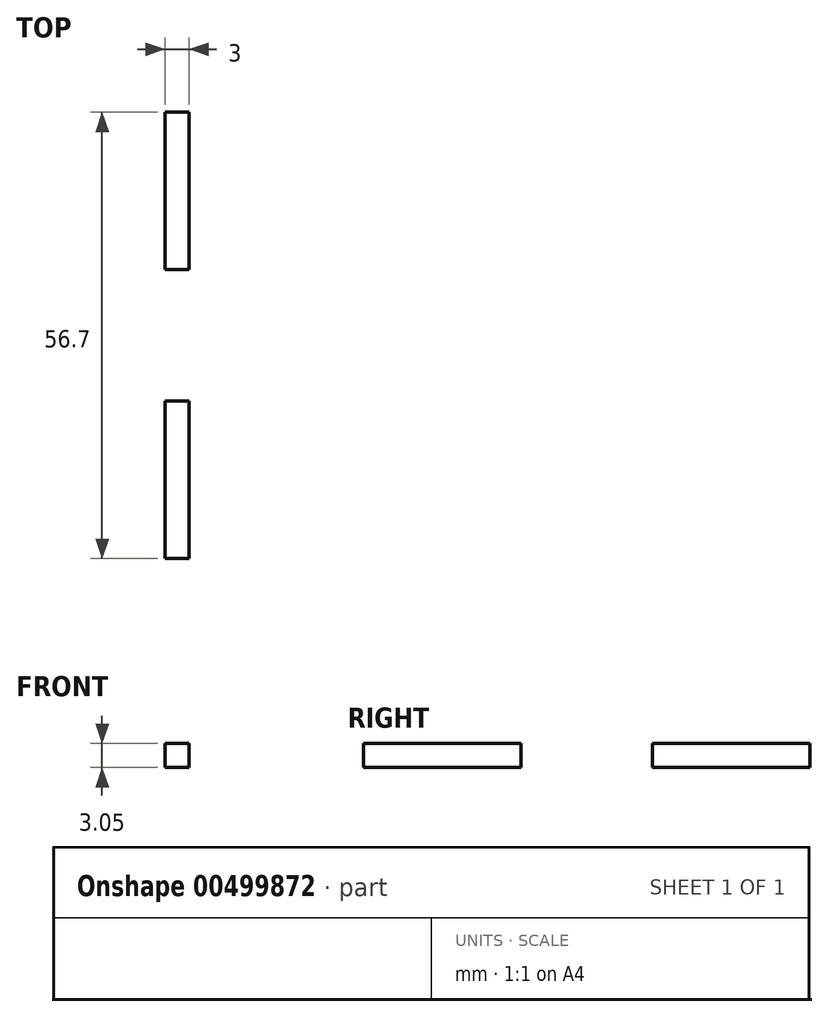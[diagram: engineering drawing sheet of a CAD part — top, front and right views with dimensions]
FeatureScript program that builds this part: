
annotation { "Feature Type Name" : "Feature", "Feature Type Description" : "" }
export const myFeature = defineFeature(function(context is Context, id is Id, definition is map)
    precondition{}
    {
        {
            var Q0;
            Q0=qCreatedBy(makeId("Right.planeOp"),FACE);
            var sketch = newSketch(context, id + "F0", { "sketchPlane" : qUnion([Q0])});
            skLineSegment(sketch, "E0.bottom", {"start": v(45, -45) * mm, "end": v(-45, -45) * mm});
            skLineSegment(sketch, "E0.top", {"start": v(45, 45) * mm, "end": v(-45, 45) * mm});
            skLineSegment(sketch, "E0.left", {"start": v(45, -45) * mm, "end": v(45, 45) * mm});
            skLineSegment(sketch, "E0.right", {"start": v(-45, -45) * mm, "end": v(-45, 45) * mm});
            skPoint(sketch, "E0.middle", {"position": v(0, 0) * mm});
            skLineSegment(sketch, "E1.bottom", {"start": v(-8.35, -48.05) * mm, "end": v(-28.35, -48.05) * mm});
            skLineSegment(sketch, "E1.top", {"start": v(-8.35, -45) * mm, "end": v(-28.35, -45) * mm});
            skLineSegment(sketch, "E1.left", {"start": v(-8.35, -48.05) * mm, "end": v(-8.35, -45) * mm});
            skLineSegment(sketch, "E1.right", {"start": v(-28.35, -48.05) * mm, "end": v(-28.35, -45) * mm});
            skPoint(sketch, "E1.middle", {"position": v(-18.35, -46.52) * mm});
            skLineSegment(sketch, "E2.bottom", {"start": v(28.35, -48.05) * mm, "end": v(8.35, -48.05) * mm});
            skLineSegment(sketch, "E2.top", {"start": v(28.35, -45) * mm, "end": v(8.35, -45) * mm});
            skLineSegment(sketch, "E2.left", {"start": v(28.35, -48.05) * mm, "end": v(28.35, -45) * mm});
            skLineSegment(sketch, "E2.right", {"start": v(8.35, -48.05) * mm, "end": v(8.35, -45) * mm});
            skPoint(sketch, "E2.middle", {"position": v(18.35, -46.53) * mm});
            skLineSegment(sketch, "E3.bottom", {"start": v(-8.35, 45) * mm, "end": v(-28.35, 45) * mm});
            skLineSegment(sketch, "E3.top", {"start": v(-8.35, 48.05) * mm, "end": v(-28.35, 48.05) * mm});
            skLineSegment(sketch, "E3.left", {"start": v(-8.35, 45) * mm, "end": v(-8.35, 48.05) * mm});
            skLineSegment(sketch, "E3.right", {"start": v(-28.35, 45) * mm, "end": v(-28.35, 48.05) * mm});
            skPoint(sketch, "E3.middle", {"position": v(-18.35, 46.53) * mm});
            skLineSegment(sketch, "E4.bottom", {"start": v(28.35, 45) * mm, "end": v(8.35, 45) * mm});
            skLineSegment(sketch, "E4.top", {"start": v(28.35, 48.05) * mm, "end": v(8.35, 48.05) * mm});
            skLineSegment(sketch, "E4.left", {"start": v(28.35, 45) * mm, "end": v(28.35, 48.05) * mm});
            skLineSegment(sketch, "E4.right", {"start": v(8.35, 45) * mm, "end": v(8.35, 48.05) * mm});
            skPoint(sketch, "E4.middle", {"position": v(18.35, 46.52) * mm});
            skLineSegment(sketch, "E5.bottom", {"start": v(-41.95, 8.4) * mm, "end": v(-45, 8.4) * mm});
            skLineSegment(sketch, "E5.top", {"start": v(-41.95, 28.3) * mm, "end": v(-45, 28.3) * mm});
            skLineSegment(sketch, "E5.left", {"start": v(-41.95, 8.4) * mm, "end": v(-41.95, 28.3) * mm});
            skLineSegment(sketch, "E5.right", {"start": v(-45, 8.4) * mm, "end": v(-45, 28.3) * mm});
            skPoint(sketch, "E5.middle", {"position": v(-43.48, 18.35) * mm});
            skLineSegment(sketch, "E6.bottom", {"start": v(-41.95, -28.3) * mm, "end": v(-45, -28.3) * mm});
            skLineSegment(sketch, "E6.top", {"start": v(-41.95, -8.4) * mm, "end": v(-45, -8.4) * mm});
            skLineSegment(sketch, "E6.left", {"start": v(-41.95, -28.3) * mm, "end": v(-41.95, -8.4) * mm});
            skLineSegment(sketch, "E6.right", {"start": v(-45, -28.3) * mm, "end": v(-45, -8.4) * mm});
            skPoint(sketch, "E6.middle", {"position": v(-43.48, -18.35) * mm});
            skLineSegment(sketch, "E7.bottom", {"start": v(45, 8.4) * mm, "end": v(41.95, 8.4) * mm});
            skLineSegment(sketch, "E7.top", {"start": v(45, 28.3) * mm, "end": v(41.95, 28.3) * mm});
            skLineSegment(sketch, "E7.left", {"start": v(45, 8.4) * mm, "end": v(45, 28.3) * mm});
            skLineSegment(sketch, "E7.right", {"start": v(41.95, 8.4) * mm, "end": v(41.95, 28.3) * mm});
            skPoint(sketch, "E7.middle", {"position": v(43.47, 18.35) * mm});
            skLineSegment(sketch, "E8.bottom", {"start": v(45, -28.3) * mm, "end": v(41.95, -28.3) * mm});
            skLineSegment(sketch, "E8.top", {"start": v(45, -8.4) * mm, "end": v(41.95, -8.4) * mm});
            skLineSegment(sketch, "E8.left", {"start": v(45, -28.3) * mm, "end": v(45, -8.4) * mm});
            skLineSegment(sketch, "E8.right", {"start": v(41.95, -28.3) * mm, "end": v(41.95, -8.4) * mm});
            skPoint(sketch, "E8.middle", {"position": v(43.47, -18.35) * mm});
            skSolve(sketch);
        }
        {
            var Q0;
            {var subQ14=sQuery(id+"F0.wireOp",EDGE,"E1.top");Q0=makeQuery(id+"F0.imprint","IMPRINT",FACE,{"disambiguationData":[TD([[makeQuery(id+"F0.imprint","IMPRINT",EDGE,{"derivedFrom":subQ14}),-1.0]])]});}
            var Q1;
            Q1=makeQuery(id+"F0.imprint","IMPRINT",FACE,{"disambiguationData":[TD([[makeQuery(id+"F0.imprint","IMPRINT",EDGE,{"derivedFrom":sQuery(id+"F0.wireOp",EDGE,"lod8E6W8-zun6-Djd3-FCWS-vj9WMZNidpZL.bottom")}),-1.0]])]});
            var Q2;
            Q2=makeQuery(id+"F0.imprint","IMPRINT",FACE,{"disambiguationData":[TD([[makeQuery(id+"F0.imprint","IMPRINT",EDGE,{"derivedFrom":sQuery(id+"F0.wireOp",EDGE,"7gunOmZB-TqCy-n5AI-Cpxm-IJzbrMUrCEj5.bottom")}),-1.0]])]});
            var Q3;
            Q3=makeQuery(id+"F0.imprint","IMPRINT",FACE,{"disambiguationData":[TD([[makeQuery(id+"F0.imprint","IMPRINT",EDGE,{"derivedFrom":sQuery(id+"F0.wireOp",EDGE,"E1.bottom")}),-1.0]])]});
            var Q4;
            Q4=makeQuery(id+"F0.imprint","IMPRINT",FACE,{"disambiguationData":[TD([[makeQuery(id+"F0.imprint","IMPRINT",EDGE,{"derivedFrom":sQuery(id+"F0.wireOp",EDGE,"E2.bottom")}),-1.0]])]});
            var Q5;
            Q5=makeQuery(id+"F0.imprint","IMPRINT",FACE,{"disambiguationData":[TD([[makeQuery(id+"F0.imprint","IMPRINT",EDGE,{"derivedFrom":sQuery(id+"F0.wireOp",EDGE,"QaLidmPP-lPlJ-XrO8-7JnV-NGOJmOLOrRNk.bottom")}),-1.0]])]});
            var Q6;
            Q6=makeQuery(id+"F0.imprint","IMPRINT",FACE,{"disambiguationData":[TD([[makeQuery(id+"F0.imprint","IMPRINT",EDGE,{"derivedFrom":sQuery(id+"F0.wireOp",EDGE,"705Ssn1d-q08v-b8Qm-CejL-Mz15Mbx1QnVq.bottom")}),-1.0]])]});
            var Q7;
            Q7=makeQuery(id+"F0.imprint","IMPRINT",FACE,{"disambiguationData":[TD([[makeQuery(id+"F0.imprint","IMPRINT",EDGE,{"derivedFrom":sQuery(id+"F0.wireOp",EDGE,"E4.bottom")}),-1.0]])]});
            var Q8;
            Q8=makeQuery(id+"F0.imprint","IMPRINT",FACE,{"disambiguationData":[TD([[makeQuery(id+"F0.imprint","IMPRINT",EDGE,{"derivedFrom":sQuery(id+"F0.wireOp",EDGE,"E3.bottom")}),-1.0]])]});
            extrude(context, id + "F1", {"entities" : qUnion([Q0, Q1, Q2, Q3, Q4, Q5, Q6, Q7, Q8]), "depth" : 3 * mm, "offsetDistance" : 25 * mm});
        }
    });
